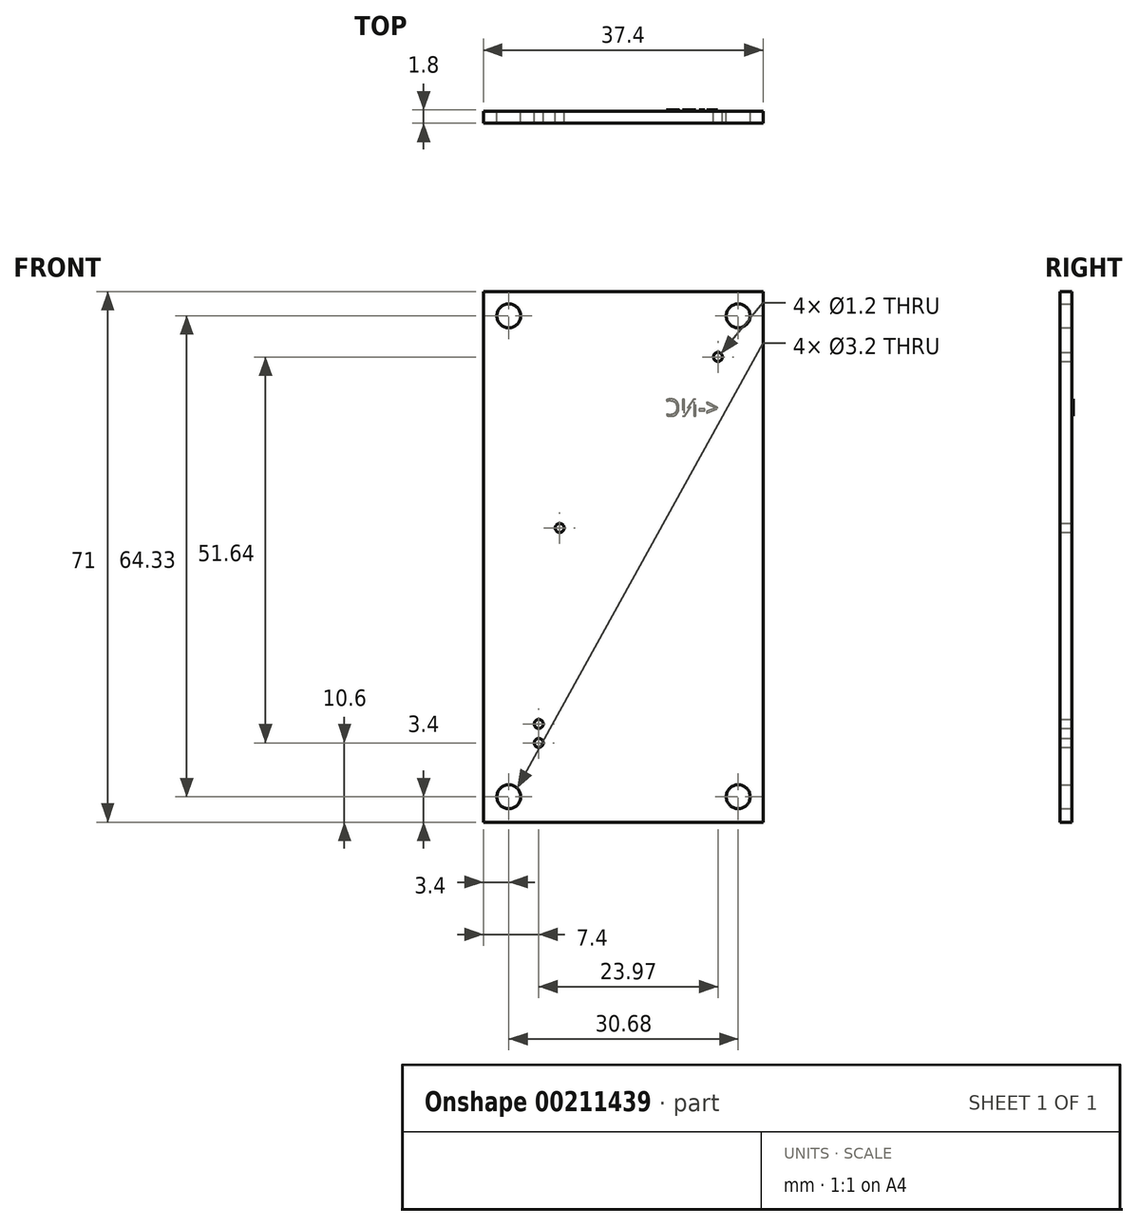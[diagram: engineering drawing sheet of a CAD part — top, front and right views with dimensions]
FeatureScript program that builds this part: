
annotation { "Feature Type Name" : "Feature", "Feature Type Description" : "" }
export const myFeature = defineFeature(function(context is Context, id is Id, definition is map)
    precondition{}
    {
        {
            var Q0;
            Q0=qCreatedBy(makeId("Front.planeOp"),FACE);
            var sketch = newSketch(context, id + "F0", { "sketchPlane" : qUnion([Q0])});
            skLineSegment(sketch, "E0.bottom", {"start": v(0, 0) * mm, "end": v(37.4, 0) * mm});
            skLineSegment(sketch, "E0.top", {"start": v(0, 71) * mm, "end": v(37.4, 71) * mm});
            skLineSegment(sketch, "E0.left", {"start": v(0, 0) * mm, "end": v(0, 71) * mm});
            skLineSegment(sketch, "E0.right", {"start": v(37.4, 0) * mm, "end": v(37.4, 71) * mm});
            skCircle(sketch, "E1", {"center": v(3.4, 67.73) * mm, "radius": 1.6 * mm});
            skCircle(sketch, "E2", {"center": v(34.08, 67.73) * mm, "radius": 1.6 * mm});
            skCircle(sketch, "E3", {"center": v(34.08, 3.4) * mm, "radius": 1.6 * mm});
            skCircle(sketch, "E4", {"center": v(3.4, 3.4) * mm, "radius": 1.6 * mm});
            skCircle(sketch, "E5", {"center": v(10.2, 39.36) * mm, "radius": 0.6 * mm});
            skCircle(sketch, "E6", {"center": v(31.37, 62.24) * mm, "radius": 0.6 * mm});
            skCircle(sketch, "E7", {"center": v(7.4, 13.14) * mm, "radius": 0.6 * mm});
            skCircle(sketch, "E8", {"center": v(7.4, 10.6) * mm, "radius": 0.6 * mm});
            skSolve(sketch);
        }
        {
            var Q0;
            Q0=makeQuery(id+"F0.imprint","IMPRINT",FACE,{"disambiguationData":[TD([[makeQuery(id+"F0.imprint","IMPRINT",EDGE,{"derivedFrom":sQuery(id+"F0.wireOp",EDGE,"E0.bottom")}),1.0]])]});
            extrude(context, id + "F1", {"entities" : qUnion([Q0]), "depth" : 1.6 * mm});
        }
        {
            var Q0;
            Q0=makeQuery(id+"F1.opExtrude","CAP_FACE",FACE,{"disambiguationData":[OSD([sQuery(id+"F0.wireOp",EDGE,"E0.bottom"),sQuery(id+"F0.wireOp",EDGE,"E0.top"),sQuery(id+"F0.wireOp",EDGE,"E0.left"),sQuery(id+"F0.wireOp",EDGE,"E0.right"),sQuery(id+"F0.wireOp",EDGE,"E1"),sQuery(id+"F0.wireOp",EDGE,"E2"),sQuery(id+"F0.wireOp",EDGE,"E3"),sQuery(id+"F0.wireOp",EDGE,"E4"),sQuery(id+"F0.wireOp",EDGE,"E5"),sQuery(id+"F0.wireOp",EDGE,"E6"),sQuery(id+"F0.wireOp",EDGE,"E7"),sQuery(id+"F0.wireOp",EDGE,"E8")])],"isStart":true});
            var sketch = newSketch(context, id + "F2", { "sketchPlane" : qUnion([Q0])});
            skText(sketch, "E9", { "text": "<-NC", "fontName": "OpenSans-Regular.ttf"});
            const initialGuessF2  = {"E9": [-0.0315, 0.05434, 1, 0, 0.00226]};
            skSetInitialGuess(sketch, initialGuessF2);
            skSolve(sketch);
        }
        {
            var Q0;
            Q0 = qSketchRegion(id + "F2", true);
            extrude(context, id + "F3", {"entities" : qUnion([Q0]), "operationType" : NewBodyOperationType.ADD, "depth" : 0.2 * mm});
        }
    });
